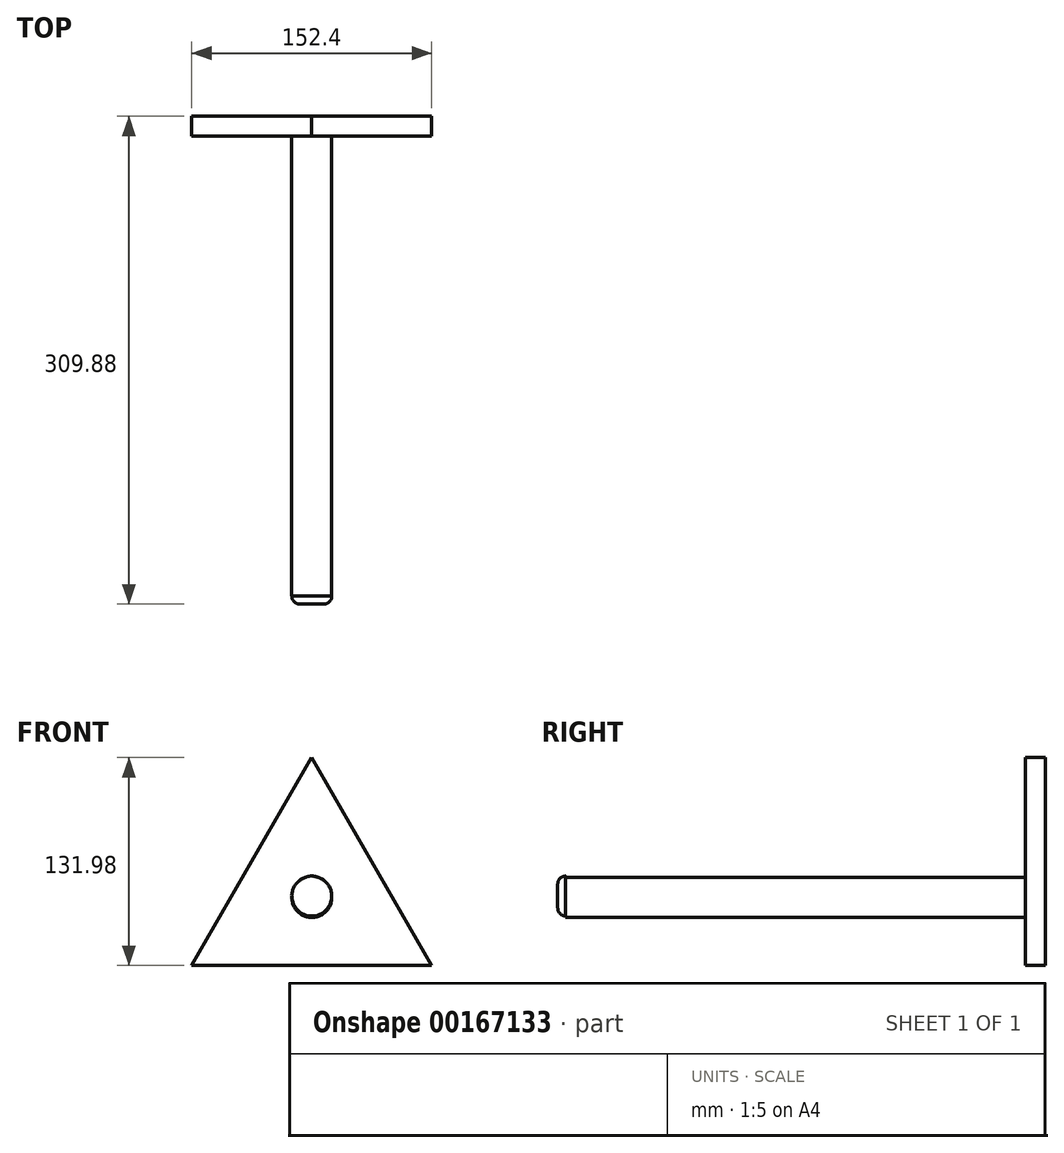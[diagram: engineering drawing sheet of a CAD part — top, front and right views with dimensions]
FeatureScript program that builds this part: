
annotation { "Feature Type Name" : "Feature", "Feature Type Description" : "" }
export const myFeature = defineFeature(function(context is Context, id is Id, definition is map)
    precondition{}
    {
        {
            var Q0;
            Q0=qCreatedBy(makeId("Front.planeOp"),FACE);
            var sketch = newSketch(context, id + "F0", { "sketchPlane" : qUnion([Q0])});
            skCircle(sketch, "E0.cCircle", {"center": v(0, 0) * mm, "radius": 44 * mm, "construction": true});
            skLineSegment(sketch, "E0.0", {"start": v(76.2, -44) * mm, "end": v(-76.2, -44) * mm});
            skLineSegment(sketch, "E0.1", {"start": v(-76.2, -44) * mm, "end": v(0, 87.99) * mm});
            skLineSegment(sketch, "E0.2", {"start": v(0, 87.99) * mm, "end": v(76.2, -44) * mm});
            skPoint(sketch, "E0.0.midPoint", {"position": v(0, -44) * mm});
            skSolve(sketch);
        }
        {
            var Q0;
            Q0 = qSketchRegion(id + "F0", true);
            extrude(context, id + "F1", {"entities" : qUnion([Q0]), "depth" : 12.7 * mm});
        }
        {
            var Q0;
            Q0=qCreatedBy(makeId("Front.planeOp"),FACE);
            var sketch = newSketch(context, id + "F2", { "sketchPlane" : qUnion([Q0])});
            skCircle(sketch, "E1", {"center": v(0, -0.9) * mm, "radius": 12.7 * mm});
            skSolve(sketch);
        }
        {
            var Q0;
            Q0 = qSketchRegion(id + "F2", true);
            extrude(context, id + "F3", {"entities" : qUnion([Q0]), "operationType" : NewBodyOperationType.ADD, "depth" : 304.8 * mm});
        }
        {
            var Q0;
            Q0=makeQuery(id+"F3.opExtrude","CAP_FACE",FACE,{"disambiguationData":[OSD([sQuery(id+"F2.wireOp",EDGE,"E1")])],"isStart":false});
            var sketch = newSketch(context, id + "F4", { "sketchPlane" : qUnion([Q0])});
            skCircle(sketch, "E2", {"center": v(0, 0) * mm, "radius": 12.7 * mm});
            skSolve(sketch);
        }
        {
            var Q0;
            Q0 = qSketchRegion(id + "F4", true);
            extrude(context, id + "F5", {"entities" : qUnion([Q0]), "operationType" : NewBodyOperationType.ADD, "depth" : 5.08 * mm});
        }
        {
            var Q0;
            Q0=makeQuery(id+"F5.opExtrude","CAP_FACE",FACE,{"disambiguationData":[OSD([sQuery(id+"F4.wireOp",EDGE,"E2")])],"isStart":false});
            fillet(context, id + "F6", {"entities" : qUnion([Q0]), "radius" : 5.08 * mm, "tangentPropagation" : true, "allowEdgeOverflow" : false});
        }
    });
